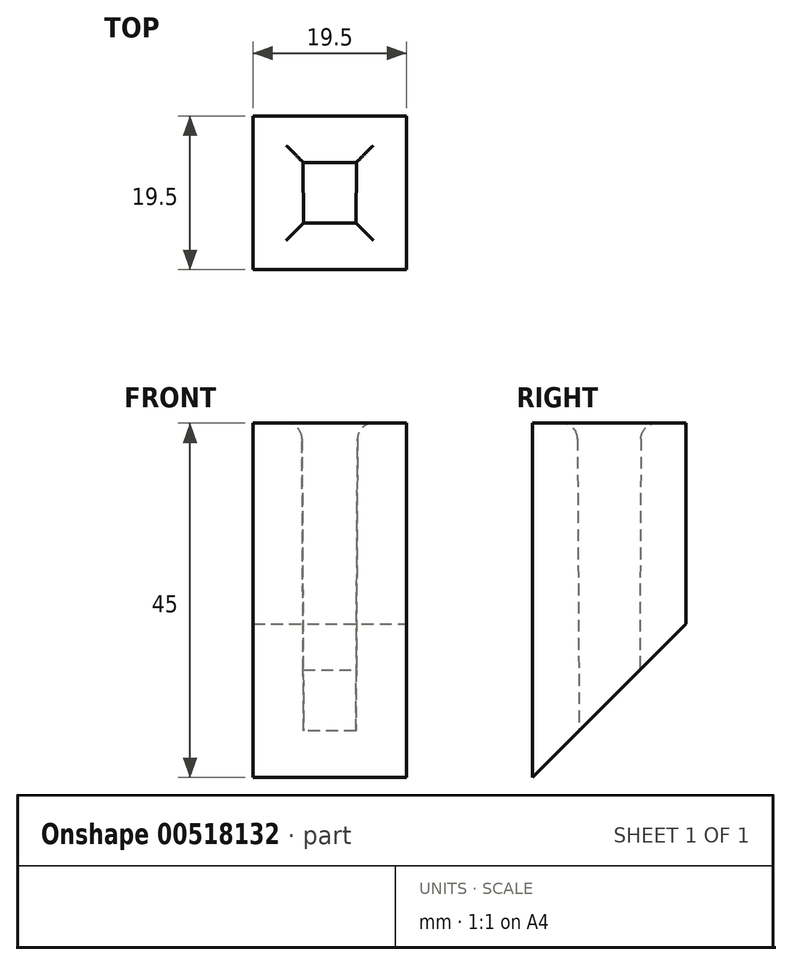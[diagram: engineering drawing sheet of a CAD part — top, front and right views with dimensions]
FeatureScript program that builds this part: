
annotation { "Feature Type Name" : "Feature", "Feature Type Description" : "" }
export const myFeature = defineFeature(function(context is Context, id is Id, definition is map)
    precondition{}
    {
        {
            var Q0;
            Q0=qCreatedBy(makeId("Top.planeOp"),FACE);
            var sketch = newSketch(context, id + "F0", { "sketchPlane" : qUnion([Q0])});
            skLineSegment(sketch, "E0.bottom", {"start": v(0, 0) * mm, "end": v(-19.5, 0) * mm});
            skLineSegment(sketch, "E0.top", {"start": v(0, -19.5) * mm, "end": v(-19.5, -19.5) * mm});
            skLineSegment(sketch, "E0.left", {"start": v(0, 0) * mm, "end": v(0, -19.5) * mm});
            skLineSegment(sketch, "E0.right", {"start": v(-19.5, 0) * mm, "end": v(-19.5, -19.5) * mm});
            skLineSegment(sketch, "E1.bottom", {"start": v(-13.05, -5.95) * mm, "end": v(-6.45, -5.95) * mm});
            skLineSegment(sketch, "E1.top", {"start": v(-13.05, -13.55) * mm, "end": v(-6.45, -13.55) * mm});
            skLineSegment(sketch, "E1.left", {"start": v(-13.05, -5.95) * mm, "end": v(-13.05, -13.55) * mm});
            skLineSegment(sketch, "E1.right", {"start": v(-6.45, -5.95) * mm, "end": v(-6.45, -13.55) * mm});
            skSolve(sketch);
        }
        {
            var Q0;
            Q0 = qSketchRegion(id + "F0", true);
            extrude(context, id + "F1", {"entities" : qUnion([Q0]), "depth" : 45 * mm, "offsetDistance" : 25 * mm});
        }
        {
            var Q0;
            Q0=makeQuery(id+"F1.opExtrude","SWEPT_FACE",FACE,{"disambiguationData":[OSD([sQuery(id+"F0.wireOp",EDGE,"E0.left")])]});
            var sketch = newSketch(context, id + "F2", { "sketchPlane" : qUnion([Q0])});
            skLineSegment(sketch, "E2", {"start": v(-19.5, 0) * mm, "end": v(0, 19.5) * mm});
            skLineSegment(sketch, "E3", {"start": v(0, 19.5) * mm, "end": v(0, 0) * mm});
            skLineSegment(sketch, "E4", {"start": v(0, 0) * mm, "end": v(-19.5, 0) * mm});
            skSolve(sketch);
        }
        {
            var Q0;
            Q0 = qSketchRegion(id + "F2", true);
            extrude(context, id + "F3", {"entities" : qUnion([Q0]), "operationType" : NewBodyOperationType.REMOVE, "oppositeDirection" : true, "depth" : 25 * mm, "offsetDistance" : 25 * mm});
        }
        {
            var Q0;
            Q0=qCreatedBy(makeId("Top.planeOp"),FACE);
            var sketch = newSketch(context, id + "F4", { "sketchPlane" : qUnion([Q0])});
            skLineSegment(sketch, "E5.bottom", {"start": v(-13.05, -5.95) * mm, "end": v(-6.45, -5.95) * mm});
            skLineSegment(sketch, "E5.top", {"start": v(-13.05, -13.55) * mm, "end": v(-6.45, -13.55) * mm});
            skLineSegment(sketch, "E5.left", {"start": v(-13.05, -5.95) * mm, "end": v(-13.05, -13.55) * mm});
            skLineSegment(sketch, "E5.right", {"start": v(-6.45, -5.95) * mm, "end": v(-6.45, -13.55) * mm});
            skSolve(sketch);
        }
        {
            var Q0;
            Q0 = qSketchRegion(id + "F4", true);
            extrude(context, id + "F5", {"entities" : qUnion([Q0]), "operationType" : NewBodyOperationType.REMOVE, "depth" : 50 * mm, "offsetDistance" : 25 * mm, "hasDraft" : true, "draftAngle" : 0.3 * degree});
        }
        {
            var Q0;
            Q0=makeQuery(id+"F5.boolean.opBoolean","INTERSECT",EDGE,{"derivedFrom":[makeQuery(id+"F1.opExtrude","CAP_FACE",FACE,{"disambiguationData":[OSD([sQuery(id+"F0.wireOp",EDGE,"E0.bottom"),sQuery(id+"F0.wireOp",EDGE,"E0.top"),sQuery(id+"F0.wireOp",EDGE,"E0.left"),sQuery(id+"F0.wireOp",EDGE,"E0.right"),sQuery(id+"F0.wireOp",EDGE,"E1.bottom"),sQuery(id+"F0.wireOp",EDGE,"E1.top"),sQuery(id+"F0.wireOp",EDGE,"E1.left"),sQuery(id+"F0.wireOp",EDGE,"E1.right")])],"isStart":false}),makeQuery(id+"F5.opExtrude","SWEPT_FACE",FACE,{"disambiguationData":[OSD([sQuery(id+"F4.wireOp",EDGE,"E5.bottom")])]})]});
            var Q1;
            Q1=makeQuery(id+"F5.boolean.opBoolean","INTERSECT",EDGE,{"derivedFrom":[makeQuery(id+"F1.opExtrude","CAP_FACE",FACE,{"disambiguationData":[OSD([sQuery(id+"F0.wireOp",EDGE,"E0.bottom"),sQuery(id+"F0.wireOp",EDGE,"E0.top"),sQuery(id+"F0.wireOp",EDGE,"E0.left"),sQuery(id+"F0.wireOp",EDGE,"E0.right"),sQuery(id+"F0.wireOp",EDGE,"E1.bottom"),sQuery(id+"F0.wireOp",EDGE,"E1.top"),sQuery(id+"F0.wireOp",EDGE,"E1.left"),sQuery(id+"F0.wireOp",EDGE,"E1.right")])],"isStart":false}),makeQuery(id+"F5.opExtrude","SWEPT_FACE",FACE,{"disambiguationData":[OSD([sQuery(id+"F4.wireOp",EDGE,"E5.left")])]})]});
            var Q2;
            Q2=makeQuery(id+"F5.boolean.opBoolean","INTERSECT",EDGE,{"derivedFrom":[makeQuery(id+"F1.opExtrude","CAP_FACE",FACE,{"disambiguationData":[OSD([sQuery(id+"F0.wireOp",EDGE,"E0.bottom"),sQuery(id+"F0.wireOp",EDGE,"E0.top"),sQuery(id+"F0.wireOp",EDGE,"E0.left"),sQuery(id+"F0.wireOp",EDGE,"E0.right"),sQuery(id+"F0.wireOp",EDGE,"E1.bottom"),sQuery(id+"F0.wireOp",EDGE,"E1.top"),sQuery(id+"F0.wireOp",EDGE,"E1.left"),sQuery(id+"F0.wireOp",EDGE,"E1.right")])],"isStart":false}),makeQuery(id+"F5.opExtrude","SWEPT_FACE",FACE,{"disambiguationData":[OSD([sQuery(id+"F4.wireOp",EDGE,"E5.right")])]})]});
            var Q3;
            Q3=makeQuery(id+"F5.boolean.opBoolean","INTERSECT",EDGE,{"derivedFrom":[makeQuery(id+"F1.opExtrude","CAP_FACE",FACE,{"disambiguationData":[OSD([sQuery(id+"F0.wireOp",EDGE,"E0.bottom"),sQuery(id+"F0.wireOp",EDGE,"E0.top"),sQuery(id+"F0.wireOp",EDGE,"E0.left"),sQuery(id+"F0.wireOp",EDGE,"E0.right"),sQuery(id+"F0.wireOp",EDGE,"E1.bottom"),sQuery(id+"F0.wireOp",EDGE,"E1.top"),sQuery(id+"F0.wireOp",EDGE,"E1.left"),sQuery(id+"F0.wireOp",EDGE,"E1.right")])],"isStart":false}),makeQuery(id+"F5.opExtrude","SWEPT_FACE",FACE,{"disambiguationData":[OSD([sQuery(id+"F4.wireOp",EDGE,"E5.top")])]})]});
            fillet(context, id + "F6", {"entities" : qUnion([Q0, Q1, Q2, Q3]), "tangentPropagation" : true, "radius" : 2 * mm, "defaultsChanged" : true, "vertexSettings" : [], "allowEdgeOverflow" : false});
        }
    });
